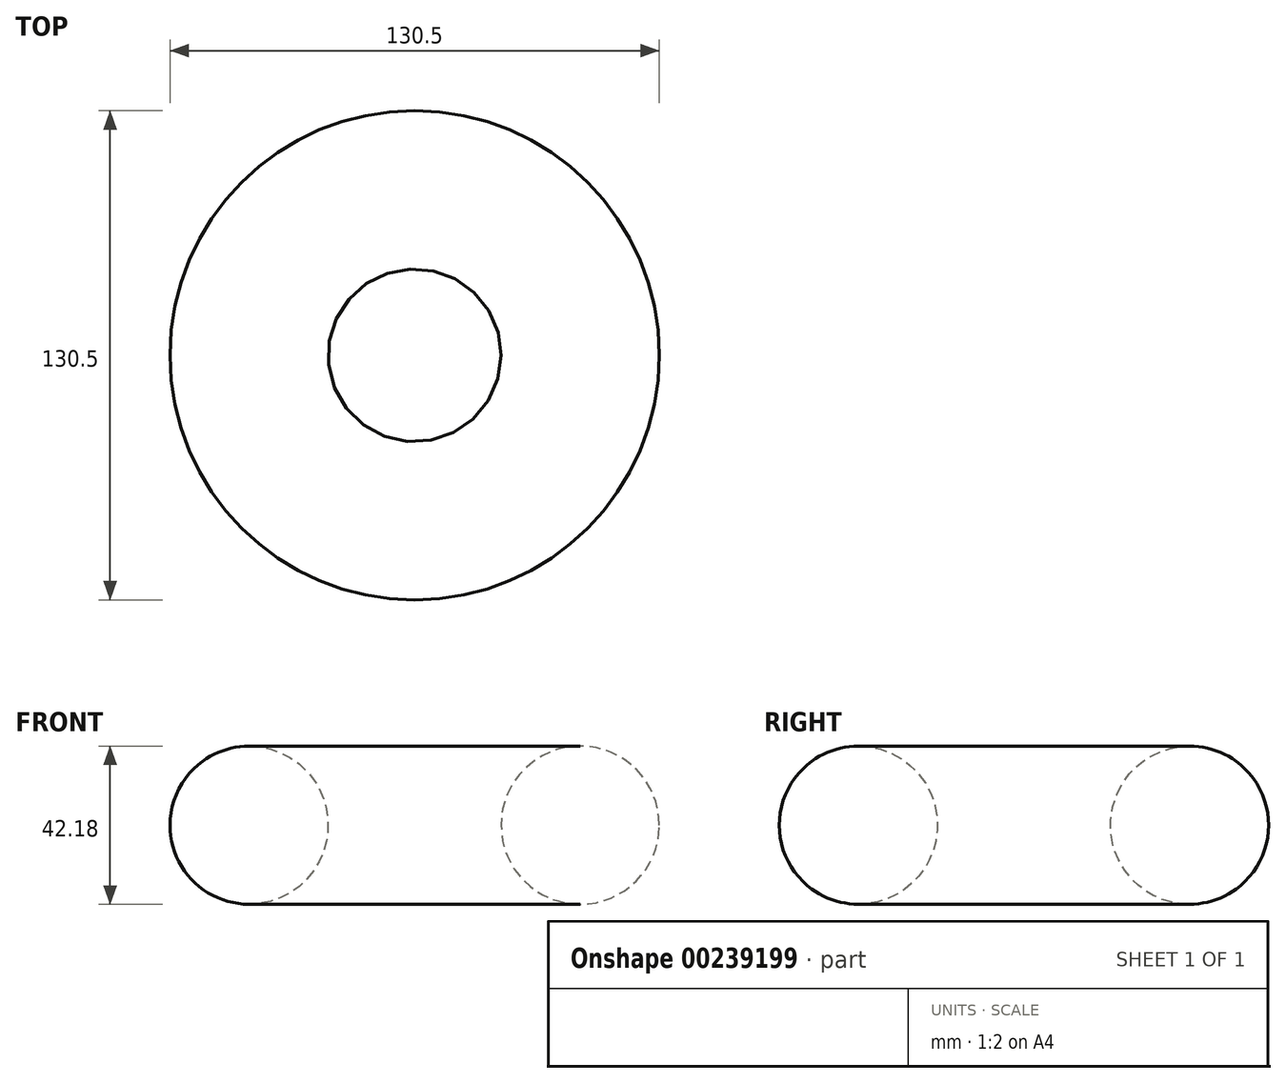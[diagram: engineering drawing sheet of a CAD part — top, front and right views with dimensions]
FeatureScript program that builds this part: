
annotation { "Feature Type Name" : "Feature", "Feature Type Description" : "" }
export const myFeature = defineFeature(function(context is Context, id is Id, definition is map)
    precondition{}
    {
        {
            var Q0;
            Q0=qCreatedBy(makeId("Front.planeOp"),FACE);
            var sketch = newSketch(context, id + "F0", { "sketchPlane" : qUnion([Q0])});
            skCircle(sketch, "E0", {"center": v(-44.16, 0) * mm, "radius": 21.1 * mm});
            skLineSegment(sketch, "E1", {"start": v(0, 39.8) * mm, "end": v(0, -42.06) * mm, "construction": true});
            skSolve(sketch);
        }
        {
            var Q0;
            Q0=makeQuery(id+"F0.imprint","IMPRINT",FACE,{"disambiguationData":[TD([[makeQuery(id+"F0.imprint","IMPRINT",EDGE,{"derivedFrom":sQuery(id+"F0.wireOp",EDGE,"E0")}),1.0]])]});
            var Q1;
            Q1=sQuery(id+"F0.wireOp",EDGE,"E1");
            revolve(context, id + "F1", {"entities" : qUnion([Q0]), "axis" : qUnion([Q1]), "revolveType" : RevolveType.FULL});
        }
    });
